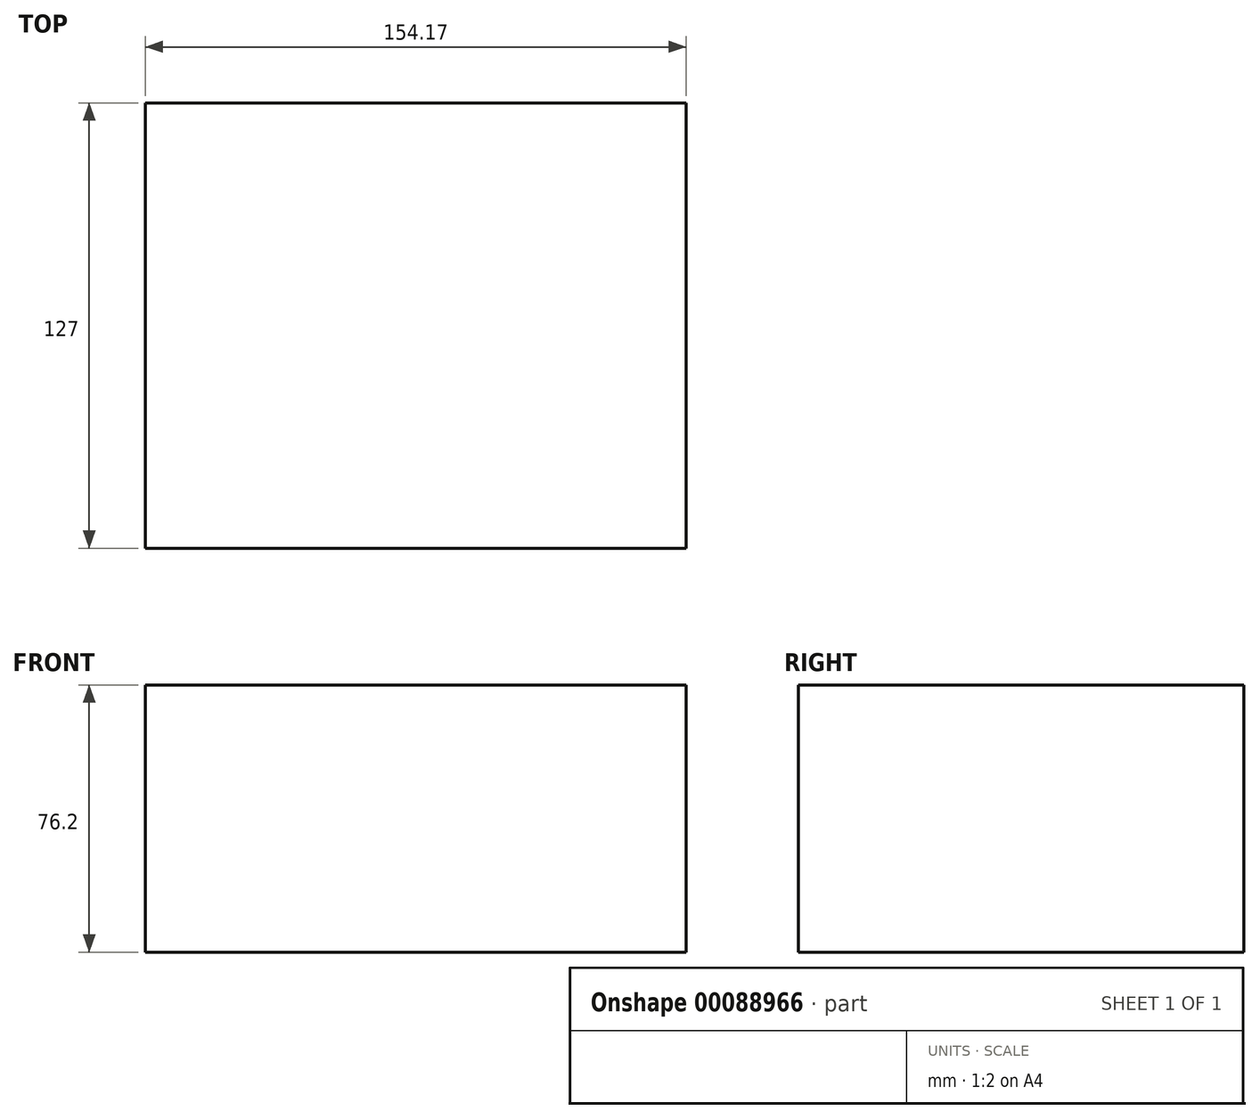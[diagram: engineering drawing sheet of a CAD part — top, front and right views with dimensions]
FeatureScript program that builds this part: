
annotation { "Feature Type Name" : "Feature", "Feature Type Description" : "" }
export const myFeature = defineFeature(function(context is Context, id is Id, definition is map)
    precondition{}
    {
        {
            var Q0;
            Q0=qCreatedBy(makeId("Front.planeOp"),FACE);
            var sketch = newSketch(context, id + "F0", { "sketchPlane" : qUnion([Q0])});
            skLineSegment(sketch, "E0.bottom", {"start": v(42.25, 65.8) * mm, "end": v(-111.92, 65.8) * mm});
            skLineSegment(sketch, "E0.top", {"start": v(42.25, -10.4) * mm, "end": v(-111.92, -10.4) * mm});
            skLineSegment(sketch, "E0.left", {"start": v(42.25, 65.8) * mm, "end": v(42.25, -10.4) * mm});
            skLineSegment(sketch, "E0.right", {"start": v(-111.92, 65.8) * mm, "end": v(-111.92, -10.4) * mm});
            skPoint(sketch, "E0.middle", {"position": v(-34.84, 27.7) * mm});
            skSolve(sketch);
        }
        {
            var Q0;
            Q0=makeQuery(id+"F0.imprint","IMPRINT",FACE,{"disambiguationData":[TD([[makeQuery(id+"F0.imprint","IMPRINT",EDGE,{"derivedFrom":sQuery(id+"F0.wireOp",EDGE,"E0.bottom")}),1.0]])]});
            extrude(context, id + "F1", {"entities" : qUnion([Q0]), "depth" : 127 * mm});
        }
    });
